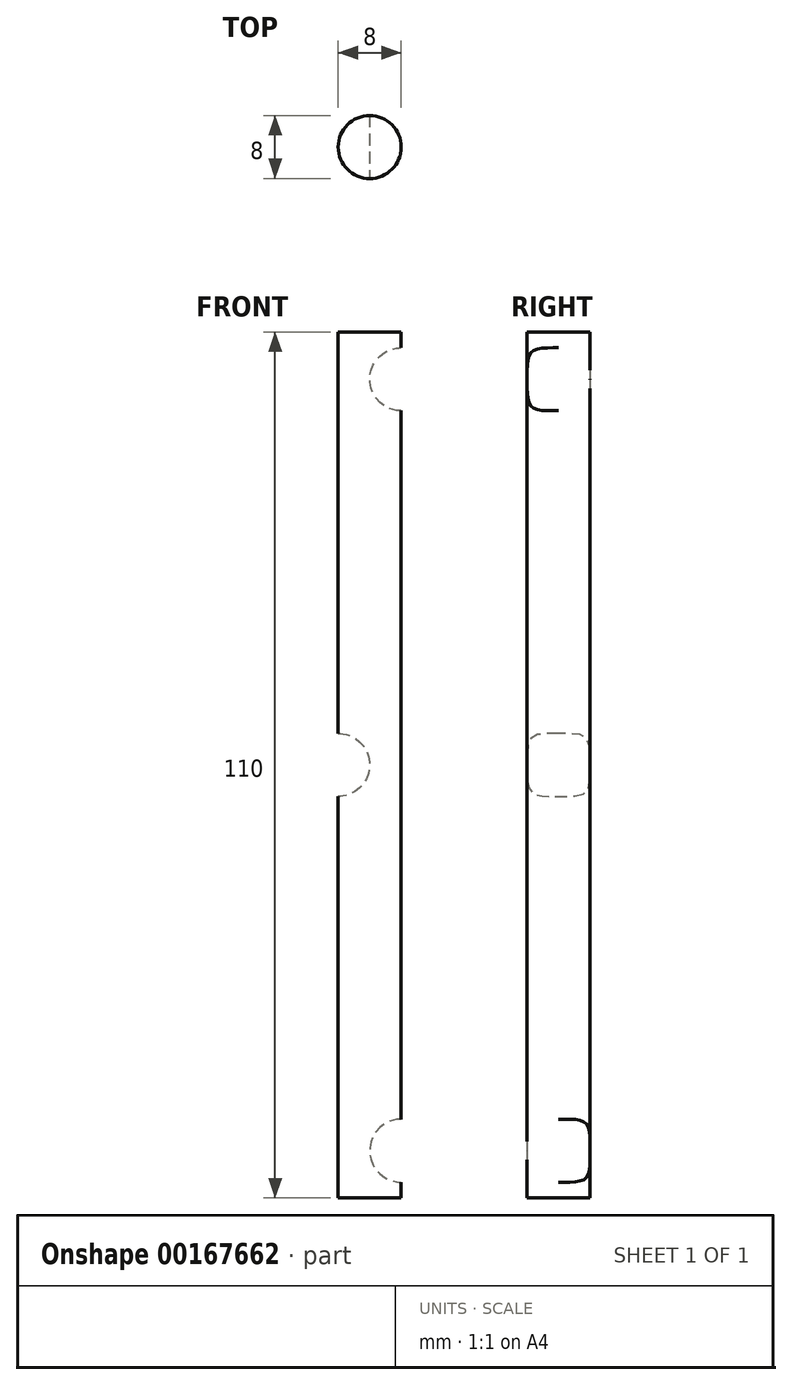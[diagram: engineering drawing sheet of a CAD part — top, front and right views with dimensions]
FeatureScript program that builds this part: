
annotation { "Feature Type Name" : "Feature", "Feature Type Description" : "" }
export const myFeature = defineFeature(function(context is Context, id is Id, definition is map)
    precondition{}
    {
        {
            var Q0;
            Q0=qCreatedBy(makeId("Top.planeOp"),FACE);
            var sketch = newSketch(context, id + "F0", { "sketchPlane" : qUnion([Q0])});
            skCircle(sketch, "E0", {"center": v(0, 0) * mm, "radius": 4 * mm});
            skSolve(sketch);
        }
        {
            var Q0;
            Q0=makeQuery(id+"F0.imprint","IMPRINT",FACE,{"disambiguationData":[TD([[makeQuery(id+"F0.imprint","IMPRINT",EDGE,{"derivedFrom":sQuery(id+"F0.wireOp",EDGE,"E0")}),1.0]])]});
            extrude(context, id + "F1", {"entities" : qUnion([Q0]), "depth" : 110 * mm});
        }
        {
            var Q0;
            Q0=qCreatedBy(makeId("Top.planeOp"),FACE);
            var sketch = newSketch(context, id + "F2", { "sketchPlane" : qUnion([Q0])});
            skCircle(sketch, "E1", {"center": v(0, 0) * mm, "radius": 4 * mm});
            skSolve(sketch);
        }
        {
            var Q0;
            Q0=makeQuery(id+"F2.imprint","IMPRINT",FACE,{"disambiguationData":[TD([[makeQuery(id+"F2.imprint","IMPRINT",EDGE,{"derivedFrom":sQuery(id+"F2.wireOp",EDGE,"E1")}),1.0]])]});
            extrude(context, id + "F3", {"entities" : qUnion([Q0]), "depth" : 110 * mm});
        }
        {
            var Q0;
            Q0=qCreatedBy(makeId("Front.planeOp"),FACE);
            cPlane(context, id + "F4", {"entities" : qUnion([Q0]), "cplaneType" : CPlaneType.OFFSET, "offset" : 4 * mm, "width" : 150 * mm, "height" : 150 * mm});
        }
        {
            var Q0;
            Q0=qCreatedBy(id+"F4.planeOp",FACE);
            var sketch = newSketch(context, id + "F5", { "sketchPlane" : qUnion([Q0])});
            skLineSegment(sketch, "E2", {"start": v(-4, 0) * mm, "end": v(-4, 110) * mm});
            skLineSegment(sketch, "E3", {"start": v(4, 110) * mm, "end": v(4, 0) * mm});
            skArc(sketch, "E4", {"start": v(4, 108) * mm, "mid": v(0, 104) * mm, "end": v(4, 100) * mm});
            skLineSegment(sketch, "E5", {"start": v(4, 108) * mm, "end": v(4, 100) * mm});
            skLineSegment(sketch, "E6", {"start": v(4, 110) * mm, "end": v(-4, 110) * mm});
            skArc(sketch, "E7", {"start": v(-4, 51) * mm, "mid": v(0, 55) * mm, "end": v(-4, 59) * mm});
            skLineSegment(sketch, "E8", {"start": v(-4, 59) * mm, "end": v(-4, 51) * mm});
            skArc(sketch, "E9", {"start": v(4, 10) * mm, "mid": v(0, 6) * mm, "end": v(4, 2) * mm});
            skLineSegment(sketch, "E10", {"start": v(4, 10) * mm, "end": v(4, 2) * mm});
            skLineSegment(sketch, "E11", {"start": v(-4, 0) * mm, "end": v(4, 0) * mm});
            skLineSegment(sketch, "E12.0", {"start": v(-4, 110) * mm, "end": v(4, 110) * mm});
            skSolve(sketch);
        }
        {
            var Q0;
            {var subQ0=sQuery(id+"F5.wireOp",EDGE,"E4");Q0=makeQuery(id+"F5.imprint","IMPRINT",FACE,{"disambiguationData":[TD([[makeQuery(id+"F5.imprint","IMPRINT",EDGE,{"derivedFrom":subQ0}),1.0]])]});}
            var Q1;
            {var subQ0=sQuery(id+"F5.wireOp",EDGE,"E7");Q1=makeQuery(id+"F5.imprint","IMPRINT",FACE,{"disambiguationData":[TD([[makeQuery(id+"F5.imprint","IMPRINT",EDGE,{"derivedFrom":subQ0}),1.0]])]});}
            var Q2;
            {var subQ0=sQuery(id+"F5.wireOp",EDGE,"E9");Q2=makeQuery(id+"F5.imprint","IMPRINT",FACE,{"disambiguationData":[TD([[makeQuery(id+"F5.imprint","IMPRINT",EDGE,{"derivedFrom":subQ0}),1.0]])]});}
            extrude(context, id + "F6", {"entities" : qUnion([Q0, Q1, Q2]), "operationType" : NewBodyOperationType.REMOVE, "oppositeDirection" : true, "depth" : 25 * mm});
        }
    });
